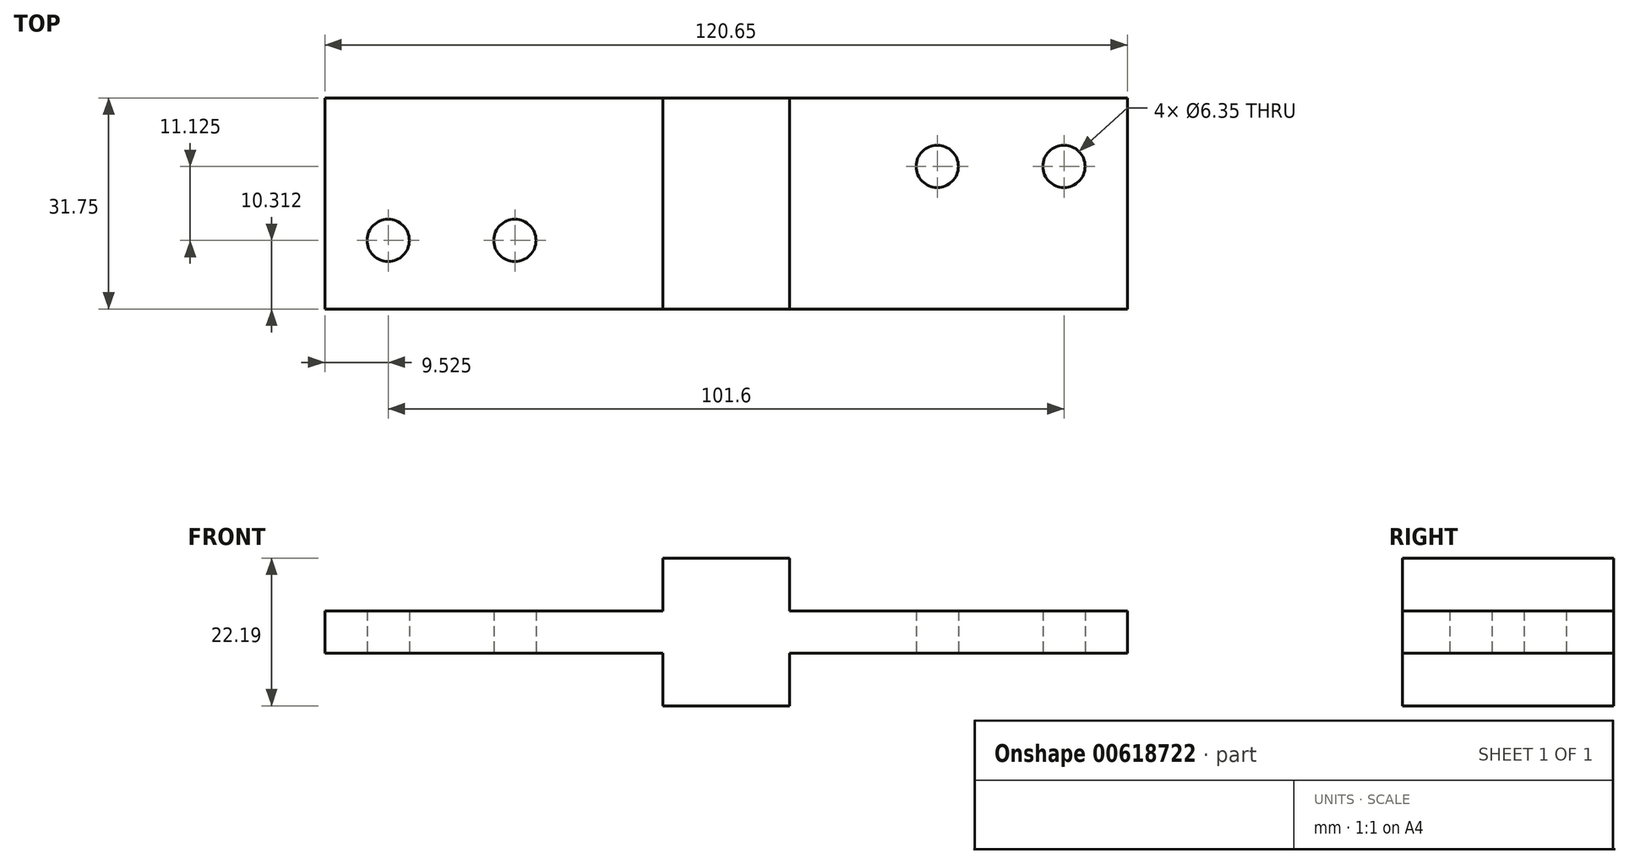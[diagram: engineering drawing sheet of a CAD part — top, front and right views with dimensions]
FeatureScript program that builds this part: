
annotation { "Feature Type Name" : "Feature", "Feature Type Description" : "" }
export const myFeature = defineFeature(function(context is Context, id is Id, definition is map)
    precondition{}
    {
        {
            var Q0;
            Q0=qCreatedBy(makeId("Front.planeOp"),FACE);
            var sketch = newSketch(context, id + "F0", { "sketchPlane" : qUnion([Q0])});
            skLineSegment(sketch, "E0", {"start": v(0, 0) * mm, "end": v(0, 6.35) * mm});
            skLineSegment(sketch, "E1", {"start": v(0, 6.35) * mm, "end": v(-50.8, 6.35) * mm});
            skLineSegment(sketch, "E2", {"start": v(-50.8, 6.35) * mm, "end": v(-50.8, 14.27) * mm});
            skLineSegment(sketch, "E3", {"start": v(-50.8, 14.27) * mm, "end": v(-69.85, 14.27) * mm});
            skLineSegment(sketch, "E4", {"start": v(-69.85, 14.27) * mm, "end": v(-69.85, 6.35) * mm});
            skLineSegment(sketch, "E5", {"start": v(-69.85, 6.35) * mm, "end": v(-120.65, 6.35) * mm});
            skLineSegment(sketch, "E6", {"start": v(-120.65, 6.35) * mm, "end": v(-120.65, 0) * mm});
            skLineSegment(sketch, "E7", {"start": v(-120.65, 0) * mm, "end": v(-69.85, 0) * mm});
            skLineSegment(sketch, "E8", {"start": v(-69.85, 0) * mm, "end": v(-69.85, -7.92) * mm});
            skLineSegment(sketch, "E9", {"start": v(-69.85, -7.92) * mm, "end": v(-50.8, -7.92) * mm});
            skLineSegment(sketch, "E10", {"start": v(-50.8, -7.92) * mm, "end": v(-50.8, 0) * mm});
            skLineSegment(sketch, "E11", {"start": v(-50.8, 0) * mm, "end": v(0, 0) * mm});
            skSolve(sketch);
        }
        {
            var Q0;
            Q0 = qSketchRegion(id + "F0", true);
            extrude(context, id + "F1", {"entities" : qUnion([Q0]), "depth" : 31.75 * mm, "offsetDistance" : 25.4 * mm});
        }
        {
            var Q0;
            Q0=qCreatedBy(makeId("Top.planeOp"),FACE);
            var sketch = newSketch(context, id + "F2", { "sketchPlane" : qUnion([Q0])});
            skCircle(sketch, "E12", {"center": v(-9.53, -10.31) * mm, "radius": 3.81 * mm});
            skCircle(sketch, "E13", {"center": v(-28.58, -10.31) * mm, "radius": 3.81 * mm});
            skCircle(sketch, "E14", {"center": v(-111.12, -21.44) * mm, "radius": 3.81 * mm});
            skCircle(sketch, "E15", {"center": v(-92.08, -21.44) * mm, "radius": 3.81 * mm});
            skSolve(sketch);
        }
        {
            var Q0;
            Q0=sQuery(id+"F2.wireOp",VERTEX,"E14.center");
            var Q1;
            Q1=sQuery(id+"F2.wireOp",VERTEX,"E15.center");
            var Q2;
            Q2=sQuery(id+"F2.wireOp",VERTEX,"E13.center");
            var Q3;
            Q3=sQuery(id+"F2.wireOp",VERTEX,"E12.center");
            var Q4;
            Q4=makeQuery(id+"F1.opExtrude","SWEPT_BODY",BODY,{"disambiguationData":[OSD([sQuery(id+"F0.wireOp",EDGE,"E0"),sQuery(id+"F0.wireOp",EDGE,"E1"),sQuery(id+"F0.wireOp",EDGE,"E2"),sQuery(id+"F0.wireOp",EDGE,"E3"),sQuery(id+"F0.wireOp",EDGE,"E4"),sQuery(id+"F0.wireOp",EDGE,"E5"),sQuery(id+"F0.wireOp",EDGE,"E6"),sQuery(id+"F0.wireOp",EDGE,"E7"),sQuery(id+"F0.wireOp",EDGE,"E8"),sQuery(id+"F0.wireOp",EDGE,"E9"),sQuery(id+"F0.wireOp",EDGE,"E10"),sQuery(id+"F0.wireOp",EDGE,"E11")])]});
            hole(context, id + "F3", {"style" : HoleStyle.SIMPLE, "endStyle" : HoleEndStyle.THROUGH, "oppositeDirection" : true, "holeDiameter" : 6.35 * mm, "majorDiameter" : 6.35 * mm, "isTappedThrough" : true, "tappedDepth" : 12.7 * mm, "tapClearance" : 3, "locations" : qUnion([Q0, Q1, Q2, Q3]), "scope" : qUnion([Q4])});
        }
    });
